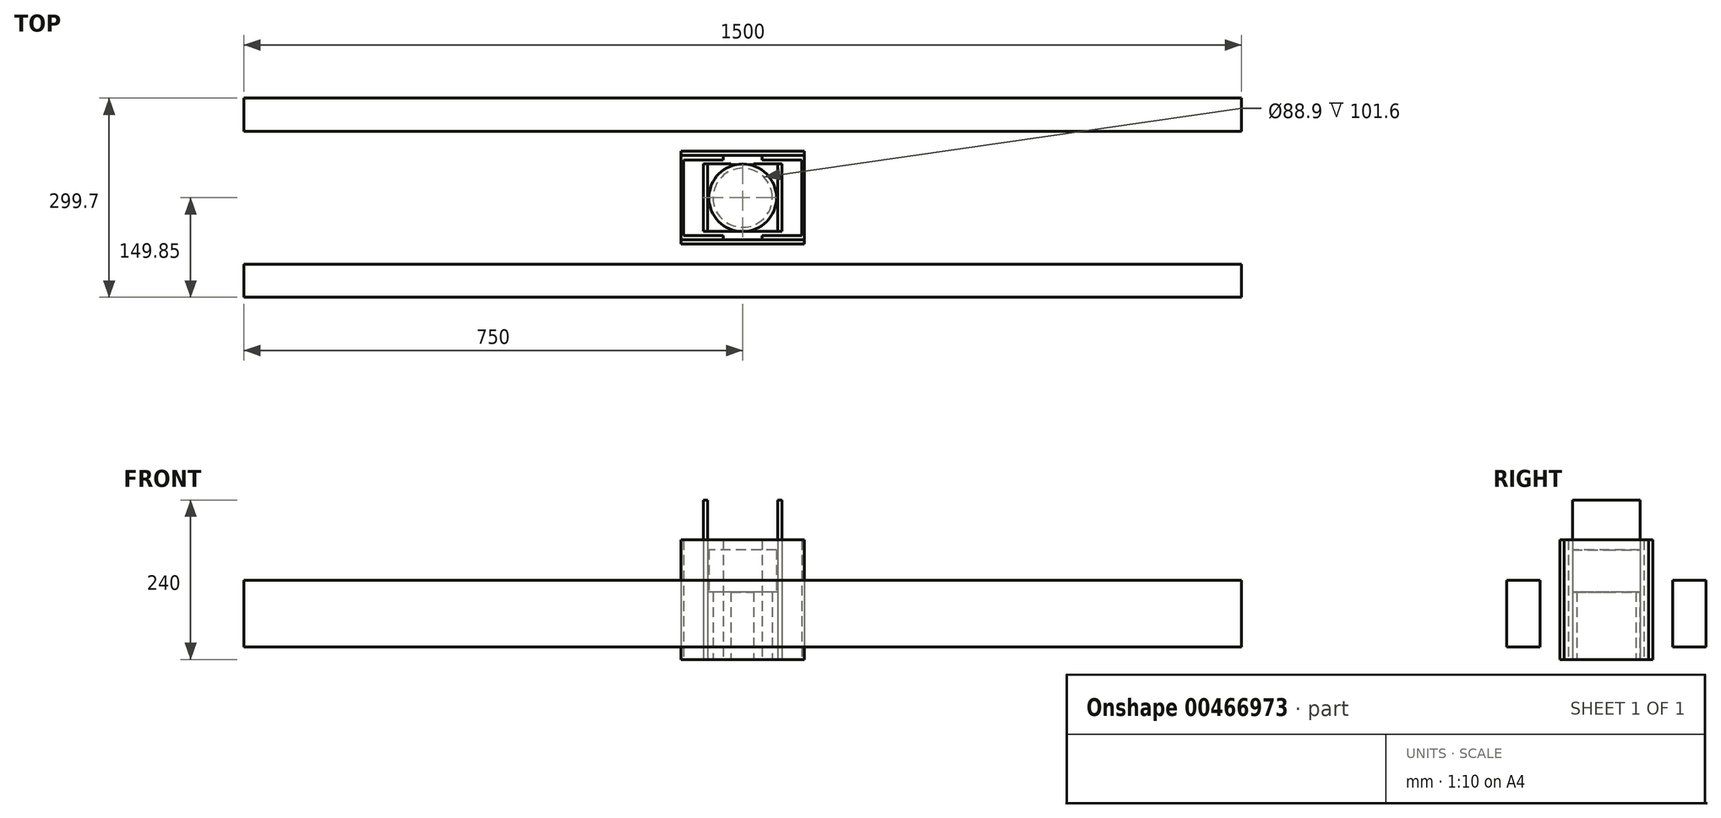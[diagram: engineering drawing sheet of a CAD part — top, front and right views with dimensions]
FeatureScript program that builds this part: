
annotation { "Feature Type Name" : "Feature", "Feature Type Description" : "" }
export const myFeature = defineFeature(function(context is Context, id is Id, definition is map)
    precondition{}
    {
        {
            var Q0;
            Q0=qCreatedBy(makeId("Top.planeOp"),FACE);
            var sketch = newSketch(context, id + "F0", { "sketchPlane" : qUnion([Q0])});
            skLineSegment(sketch, "E0.bottom", {"start": v(52.8, 50.8) * mm, "end": v(-52.8, 50.8) * mm});
            skLineSegment(sketch, "E0.top", {"start": v(52.8, -50.8) * mm, "end": v(-52.8, -50.8) * mm});
            skLineSegment(sketch, "E0.left", {"start": v(52.8, 50.8) * mm, "end": v(52.8, -50.8) * mm});
            skLineSegment(sketch, "E0.right", {"start": v(-52.8, 50.8) * mm, "end": v(-52.8, -50.8) * mm});
            skPoint(sketch, "E0.middle", {"position": v(0, 0) * mm});
            skCircle(sketch, "E1", {"center": v(0, 0) * mm, "radius": 44.45 * mm});
            skCircle(sketch, "E2", {"center": v(0, 0) * mm, "radius": 50.8 * mm, "construction": true});
            skLineSegment(sketch, "E3.bottom", {"start": v(52.8, -50.8) * mm, "end": v(59.15, -50.8) * mm});
            skLineSegment(sketch, "E3.top", {"start": v(52.8, 50.8) * mm, "end": v(59.15, 50.8) * mm});
            skLineSegment(sketch, "E3.left", {"start": v(52.8, -50.8) * mm, "end": v(52.8, 50.8) * mm});
            skLineSegment(sketch, "E3.right", {"start": v(59.15, -50.8) * mm, "end": v(59.15, 50.8) * mm});
            skLineSegment(sketch, "E4.bottom", {"start": v(-52.8, -50.8) * mm, "end": v(-59.15, -50.8) * mm});
            skLineSegment(sketch, "E4.top", {"start": v(-52.8, 50.8) * mm, "end": v(-59.15, 50.8) * mm});
            skLineSegment(sketch, "E4.left", {"start": v(-52.8, -50.8) * mm, "end": v(-52.8, 50.8) * mm});
            skLineSegment(sketch, "E4.right", {"start": v(-59.15, -50.8) * mm, "end": v(-59.15, 50.8) * mm});
            skLineSegment(sketch, "E5.bottom", {"start": v(-59.15, 31.5) * mm, "end": v(-89.15, 31.5) * mm, "construction": true});
            skLineSegment(sketch, "E5.top", {"start": v(-59.15, -31.5) * mm, "end": v(-89.15, -31.5) * mm, "construction": true});
            skLineSegment(sketch, "E5.left", {"start": v(-59.15, 31.5) * mm, "end": v(-59.15, -31.5) * mm, "construction": true});
            skLineSegment(sketch, "E5.right", {"start": v(-89.15, 31.5) * mm, "end": v(-89.15, -31.5) * mm, "construction": true});
            skLineSegment(sketch, "E6", {"start": v(0, -50.8) * mm, "end": v(0, 50.8) * mm, "construction": true});
            skLineSegment(sketch, "E7.MirrorCS", {"start": v(59.15, 31.5) * mm, "end": v(89.15, 31.5) * mm, "construction": true});
            skLineSegment(sketch, "E8.MirrorCS", {"start": v(89.15, 31.5) * mm, "end": v(89.15, -31.5) * mm, "construction": true});
            skLineSegment(sketch, "E9.MirrorCS", {"start": v(59.15, -31.5) * mm, "end": v(89.15, -31.5) * mm, "construction": true});
            skLineSegment(sketch, "E10", {"start": v(-52.8, 0) * mm, "end": v(52.8, 0) * mm, "construction": true});
            skLineSegment(sketch, "E11", {"start": v(89.15, 0) * mm, "end": v(52.8, 0) * mm, "construction": true});
            skLineSegment(sketch, "E12", {"start": v(89.15, 0) * mm, "end": v(89.15, 56.9) * mm});
            skLineSegment(sketch, "E13", {"start": v(92.96, 63.5) * mm, "end": v(92.96, 0) * mm});
            skLineSegment(sketch, "E14.bottom", {"start": v(-17.78, 50.04) * mm, "end": v(16.22, 50.04) * mm});
            skLineSegment(sketch, "E14.top", {"start": v(-17.78, 62.04) * mm, "end": v(16.22, 62.04) * mm});
            skLineSegment(sketch, "E14.left", {"start": v(-17.78, 50.04) * mm, "end": v(-17.78, 62.04) * mm});
            skLineSegment(sketch, "E14.right", {"start": v(16.22, 50.04) * mm, "end": v(16.22, 62.04) * mm});
            skLineSegment(sketch, "E15", {"start": v(59.15, -10) * mm, "end": v(76.65, -10) * mm, "construction": true});
            skLineSegment(sketch, "E16.MirrorCS", {"start": v(59.15, 10) * mm, "end": v(76.65, 10) * mm, "construction": true});
            skLineSegment(sketch, "E17", {"start": v(76.65, 10) * mm, "end": v(76.65, -10) * mm, "construction": true});
            skLineSegment(sketch, "E18.bottom", {"start": v(-92.96, 63.5) * mm, "end": v(92.96, 63.5) * mm});
            skLineSegment(sketch, "E18.top", {"start": v(-92.96, 69.85) * mm, "end": v(92.96, 69.85) * mm});
            skLineSegment(sketch, "E18.left", {"start": v(-92.96, 63.5) * mm, "end": v(-92.96, 69.85) * mm});
            skLineSegment(sketch, "E18.right", {"start": v(92.96, 63.5) * mm, "end": v(92.96, 69.85) * mm});
            skLineSegment(sketch, "E19.MirrorCS", {"start": v(92.96, -63.5) * mm, "end": v(92.96, -69.85) * mm});
            skLineSegment(sketch, "E20.MirrorCS", {"start": v(-92.96, -63.5) * mm, "end": v(-92.96, -69.85) * mm});
            skLineSegment(sketch, "E21.MirrorCS", {"start": v(-92.96, -69.85) * mm, "end": v(92.96, -69.85) * mm});
            skLineSegment(sketch, "E22.MirrorCS", {"start": v(-92.96, -63.5) * mm, "end": v(92.96, -63.5) * mm});
            skLineSegment(sketch, "E23", {"start": v(89.15, 56.9) * mm, "end": v(29.46, 56.9) * mm});
            skLineSegment(sketch, "E24", {"start": v(29.46, 56.9) * mm, "end": v(29.46, 63.5) * mm});
            skLineSegment(sketch, "E25.MirrorCS", {"start": v(29.46, -56.9) * mm, "end": v(29.46, -63.5) * mm});
            skLineSegment(sketch, "E26.MirrorCS", {"start": v(89.15, -56.9) * mm, "end": v(29.46, -56.9) * mm});
            skLineSegment(sketch, "E27.MirrorCS", {"start": v(92.96, -63.5) * mm, "end": v(92.96, 0) * mm});
            skLineSegment(sketch, "E28.MirrorCS", {"start": v(89.15, 0) * mm, "end": v(89.15, -56.9) * mm});
            skLineSegment(sketch, "E29.MirrorCS", {"start": v(-29.46, 56.9) * mm, "end": v(-29.46, 63.5) * mm});
            skLineSegment(sketch, "E30.MirrorCS", {"start": v(-89.15, 56.9) * mm, "end": v(-29.46, 56.9) * mm});
            skLineSegment(sketch, "E31.MirrorCS", {"start": v(-89.15, 0) * mm, "end": v(-89.15, 56.9) * mm});
            skLineSegment(sketch, "E32.MirrorCS", {"start": v(-92.96, 63.5) * mm, "end": v(-92.96, 0) * mm});
            skLineSegment(sketch, "E33.MirrorCS", {"start": v(-89.15, 0) * mm, "end": v(-89.15, -56.9) * mm});
            skLineSegment(sketch, "E34.MirrorCS", {"start": v(-89.15, -56.9) * mm, "end": v(-29.46, -56.9) * mm});
            skLineSegment(sketch, "E35.MirrorCS", {"start": v(-92.96, -63.5) * mm, "end": v(-92.96, 0) * mm});
            skLineSegment(sketch, "E36.MirrorCS", {"start": v(-29.46, -56.9) * mm, "end": v(-29.46, -63.5) * mm});
            skSolve(sketch);
        }
        {
            var Q0;
            Q0=makeQuery(id+"F0.imprint","IMPRINT",FACE,{"disambiguationData":[TD([[makeQuery(id+"F0.imprint","IMPRINT",EDGE,{"derivedFrom":sQuery(id+"F0.wireOp",EDGE,"E1")}),1.0]])]});
            extrude(context, id + "F1", {"entities" : qUnion([Q0]), "depth" : 101.6 * mm});
        }
        {
            var Q0;
            Q0=makeQuery(id+"F1.opExtrude","CAP_FACE",FACE,{"disambiguationData":[OSD([sQuery(id+"F0.wireOp",EDGE,"E1")])],"isStart":false});
            var sketch = newSketch(context, id + "F2", { "sketchPlane" : qUnion([Q0])});
            skCircle(sketch, "E37", {"center": v(0, 0) * mm, "radius": 50.8 * mm});
            skSolve(sketch);
        }
        {
            var Q0;
            Q0=makeQuery(id+"F2.imprint","IMPRINT",FACE,{"disambiguationData":[TD([[makeQuery(id+"F2.imprint","IMPRINT",EDGE,{"derivedFrom":sQuery(id+"F2.wireOp",EDGE,"E37")}),1.0]])]});
            var Q1;
            Q1=makeQuery(id+"F2.imprint","IMPRINT",FACE,{"disambiguationData":[TD([[makeQuery(id+"F2.imprint","IMPRINT",EDGE,{"derivedFrom":makeQuery(id+"F1.opExtrude","CAP_EDGE",EDGE,{"disambiguationData":[OSD([sQuery(id+"F0.wireOp",EDGE,"E1")])],"isStart":false})}),1.0]])]});
            extrude(context, id + "F3", {"entities" : qUnion([Q0, Q1]), "operationType" : NewBodyOperationType.ADD, "depth" : 63.5 * mm});
        }
        {
            var Q0;
            Q0=makeQuery(id+"F0.imprint","IMPRINT",FACE,{"disambiguationData":[TD([[makeQuery(id+"F0.imprint","IMPRINT",EDGE,{"derivedFrom":sQuery(id+"F0.wireOp",EDGE,"E0.bottom")}),1.0]])]});
            var Q1;
            Q1=makeQuery(id+"F3.opExtrude","CAP_FACE",FACE,{"disambiguationData":[OSD([sQuery(id+"F2.wireOp",EDGE,"E37")])],"isStart":true});
            extrude(context, id + "F4", {"entities" : qUnion([Q0]), "endBound" : BoundingType.UP_TO_SURFACE, "endBoundEntityFace" : qUnion([Q1]), "depth" : 25 * mm});
        }
        {
            assignVariable(context, id + "F5", {"name" : "travelZ", "anyValue" : 60 * mm});
        }
        {
            assignVariable(context, id + "F6", {"name" : "blockZOuterDist", "anyValue" : 180 * mm});
        }
        {
            var Q0;
            {var subQ0=sQuery(id+"F0.wireOp",EDGE,"E29.MirrorCS");Q0=makeQuery(id+"F0.imprint","IMPRINT",FACE,{"disambiguationData":[TD([[makeQuery(id+"F0.imprint","IMPRINT",EDGE,{"derivedFrom":subQ0}),1.0]])]});}
            var Q1;
            Q1=makeQuery(id+"F0.imprint","IMPRINT",FACE,{"disambiguationData":[TD([[makeQuery(id+"F0.imprint","IMPRINT",EDGE,{"derivedFrom":sQuery(id+"F0.wireOp",EDGE,"E12")}),-1.0]])]});
            extrude(context, id + "F7", {"entities" : qUnion([Q0, Q1]), "depth" : getVariable(context, 'blockZOuterDist')});
        }
        {
            var Q0;
            Q0=makeQuery(id+"F0.imprint","IMPRINT",FACE,{"disambiguationData":[TD([[makeQuery(id+"F0.imprint","IMPRINT",EDGE,{"derivedFrom":sQuery(id+"F0.wireOp",EDGE,"E4.bottom")}),-1.0]])]});
            var Q1;
            Q1=makeQuery(id+"F0.imprint","IMPRINT",FACE,{"disambiguationData":[TD([[makeQuery(id+"F0.imprint","IMPRINT",EDGE,{"derivedFrom":sQuery(id+"F0.wireOp",EDGE,"E3.bottom")}),1.0]])]});
            extrude(context, id + "F8", {"entities" : qUnion([Q0, Q1]), "depth" : getVariable(context, 'blockZOuterDist') + getVariable(context, 'travelZ')});
        }
        {
            var Q0;
            Q0=makeQuery(id+"F0.imprint","IMPRINT",FACE,{"disambiguationData":[TD([[makeQuery(id+"F0.imprint","IMPRINT",EDGE,{"derivedFrom":sQuery(id+"F0.wireOp",EDGE,"E18.top")}),-1.0]])]});
            var Q1;
            {var subQ3=sQuery(id+"F0.wireOp",EDGE,"E19.MirrorCS");Q1=makeQuery(id+"F0.imprint","IMPRINT",FACE,{"disambiguationData":[TD([[makeQuery(id+"F0.imprint","IMPRINT",EDGE,{"derivedFrom":subQ3}),-1.0]])]});}
            var Q2;
            Q2=makeQuery(id+"F7.opExtrude","CAP_FACE",FACE,{"disambiguationData":[OSD([sQuery(id+"F0.wireOp",EDGE,"08c0dea9-510f-4040-a745-3b796ae982600.MirrorCS"),sQuery(id+"F0.wireOp",EDGE,"08c0dea9-510f-4040-a745-3b796ae982601.MirrorCS"),sQuery(id+"F0.wireOp",EDGE,"08c0dea9-510f-4040-a745-3b796ae982603.MirrorCS"),sQuery(id+"F0.wireOp",EDGE,"08c0dea9-510f-4040-a745-3b796ae982605.MirrorCS"),sQuery(id+"F0.wireOp",EDGE,"08c0dea9-510f-4040-a745-3b796ae982607.MirrorCS"),sQuery(id+"F0.wireOp",EDGE,"08c0dea9-510f-4040-a745-3b796ae982608.MirrorCS"),sQuery(id+"F0.wireOp",EDGE,"08c0dea9-510f-4040-a745-3b796ae982609.MirrorCS"),sQuery(id+"F0.wireOp",EDGE,"08c0dea9-510f-4040-a745-3b796ae9826010.MirrorCS"),sQuery(id+"F0.wireOp",EDGE,"E18.bottom"),sQuery(id+"F0.wireOp",EDGE,"E22.MirrorCS")])],"isStart":false});
            extrude(context, id + "F9", {"entities" : qUnion([Q0, Q1]), "endBound" : BoundingType.UP_TO_SURFACE, "endBoundEntityFace" : qUnion([Q2]), "depth" : 25 * mm});
        }
        {
            var Q0;
            Q0=qCreatedBy(makeId("Right.planeOp"),FACE);
            var sketch = newSketch(context, id + "F10", { "sketchPlane" : qUnion([Q0])});
            skLineSegment(sketch, "E38.bottom", {"start": v(-69.85, 0) * mm, "end": v(-99.85, 0) * mm, "construction": true});
            skLineSegment(sketch, "E38.top", {"start": v(-69.85, 63) * mm, "end": v(-99.85, 63) * mm, "construction": true});
            skLineSegment(sketch, "E38.left", {"start": v(-69.85, 0) * mm, "end": v(-69.85, 63) * mm, "construction": true});
            skLineSegment(sketch, "E38.right", {"start": v(-99.85, 0) * mm, "end": v(-99.85, 63) * mm, "construction": true});
            skLineSegment(sketch, "E39.bottom", {"start": v(-82.35, 41.5) * mm, "end": v(-99.85, 41.5) * mm, "construction": true});
            skLineSegment(sketch, "E39.top", {"start": v(-82.35, 21.5) * mm, "end": v(-99.85, 21.5) * mm, "construction": true});
            skLineSegment(sketch, "E39.left", {"start": v(-82.35, 41.5) * mm, "end": v(-82.35, 21.5) * mm, "construction": true});
            skLineSegment(sketch, "E39.right", {"start": v(-99.85, 41.5) * mm, "end": v(-99.85, 21.5) * mm, "construction": true});
            skPoint(sketch, "E39.middle", {"position": v(-91.1, 31.5) * mm});
            skLineSegment(sketch, "E40", {"start": v(-99.85, 31.5) * mm, "end": v(-91.1, 31.5) * mm, "construction": true});
            skLineSegment(sketch, "E41.bottom", {"start": v(-99.85, 19) * mm, "end": v(-149.85, 19) * mm});
            skLineSegment(sketch, "E41.top", {"start": v(-99.85, 119) * mm, "end": v(-149.85, 119) * mm});
            skLineSegment(sketch, "E41.left", {"start": v(-99.85, 19) * mm, "end": v(-99.85, 119) * mm});
            skLineSegment(sketch, "E41.right", {"start": v(-149.85, 19) * mm, "end": v(-149.85, 119) * mm});
            skLineSegment(sketch, "E42", {"start": v(0, 0) * mm, "end": v(0, 73.51) * mm, "construction": true});
            skLineSegment(sketch, "E43.MirrorCS", {"start": v(82.35, 41.5) * mm, "end": v(82.35, 21.5) * mm, "construction": true});
            skLineSegment(sketch, "E44.MirrorCS", {"start": v(99.85, 31.5) * mm, "end": v(91.1, 31.5) * mm, "construction": true});
            skLineSegment(sketch, "E45.MirrorCS", {"start": v(99.85, 41.5) * mm, "end": v(99.85, 21.5) * mm, "construction": true});
            skLineSegment(sketch, "E46.MirrorCS", {"start": v(82.35, 21.5) * mm, "end": v(99.85, 21.5) * mm, "construction": true});
            skLineSegment(sketch, "E47.MirrorCS", {"start": v(82.35, 41.5) * mm, "end": v(99.85, 41.5) * mm, "construction": true});
            skLineSegment(sketch, "E48.MirrorCS", {"start": v(99.85, 0) * mm, "end": v(99.85, 63) * mm, "construction": true});
            skLineSegment(sketch, "E49.MirrorCS", {"start": v(69.85, 0) * mm, "end": v(69.85, 63) * mm, "construction": true});
            skLineSegment(sketch, "E50.MirrorCS", {"start": v(69.85, 0) * mm, "end": v(99.85, 0) * mm, "construction": true});
            skLineSegment(sketch, "E51.MirrorCS", {"start": v(69.85, 63) * mm, "end": v(99.85, 63) * mm, "construction": true});
            skPoint(sketch, "E52.MirrorP", {"position": v(91.1, 31.5) * mm});
            skLineSegment(sketch, "E53.MirrorCS", {"start": v(149.85, 19) * mm, "end": v(149.85, 119) * mm});
            skLineSegment(sketch, "E54.MirrorCS", {"start": v(99.85, 19) * mm, "end": v(99.85, 119) * mm});
            skLineSegment(sketch, "E55.MirrorCS", {"start": v(99.85, 119) * mm, "end": v(149.85, 119) * mm});
            skLineSegment(sketch, "E56.MirrorCS", {"start": v(99.85, 19) * mm, "end": v(149.85, 19) * mm});
            skSolve(sketch);
        }
        {
            var Q0;
            Q0 = qSketchRegion(id + "F10", true);
            extrude(context, id + "F11", {"entities" : qUnion([Q0]), "endBound" : BoundingType.SYMMETRIC, "depth" : 1500 * mm});
        }
    });
